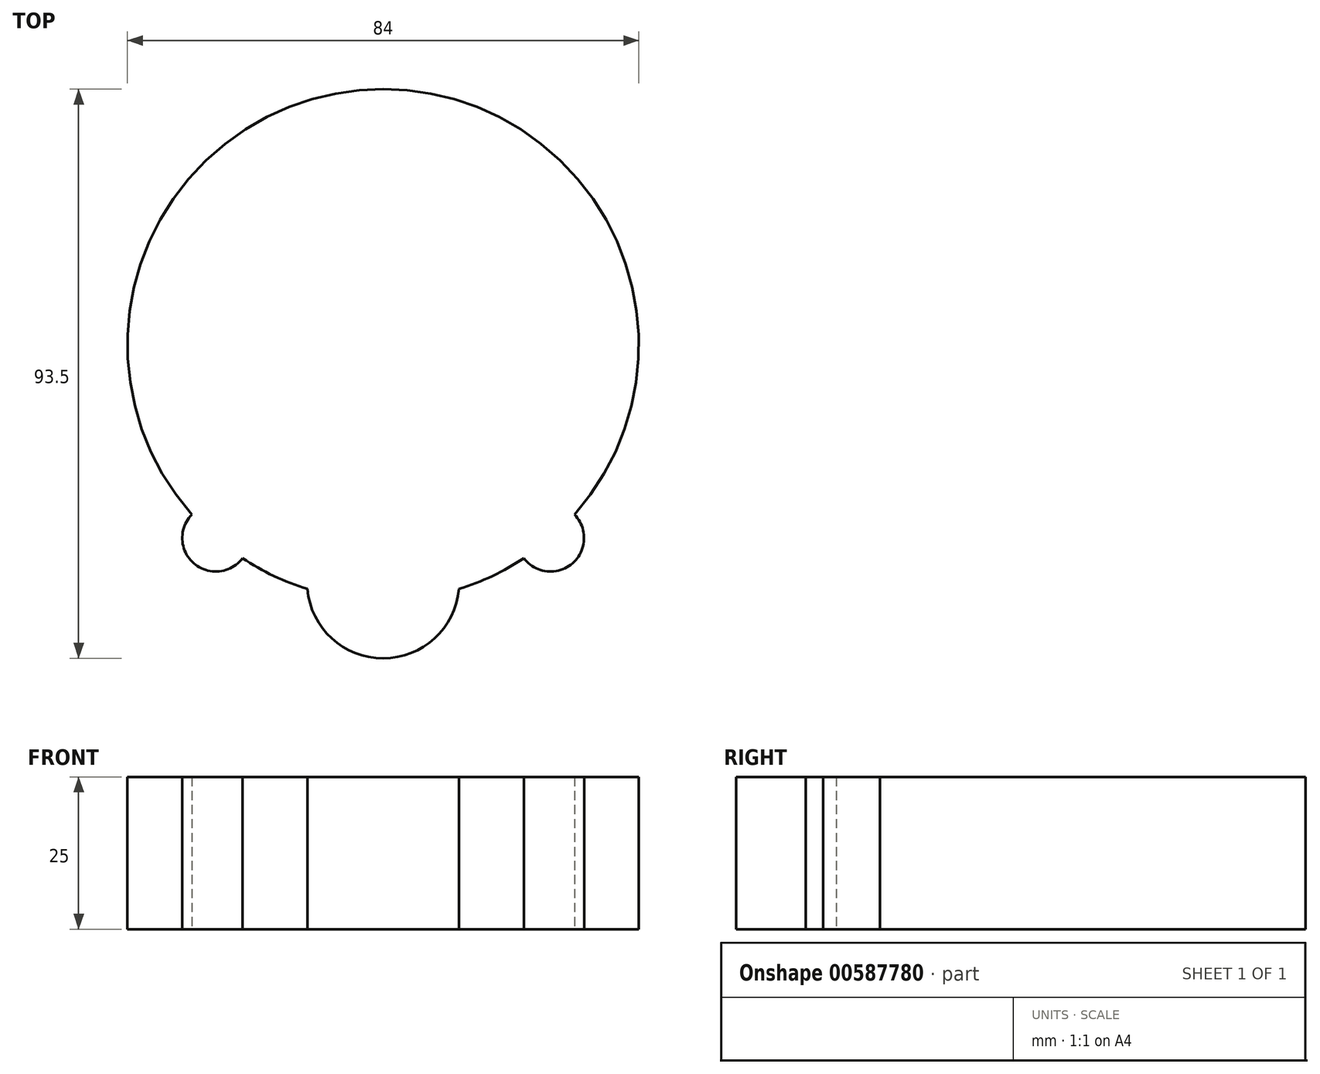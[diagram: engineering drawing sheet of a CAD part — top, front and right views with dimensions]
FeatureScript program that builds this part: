
annotation { "Feature Type Name" : "Feature", "Feature Type Description" : "" }
export const myFeature = defineFeature(function(context is Context, id is Id, definition is map)
    precondition{}
    {
        {
            var Q0;
            Q0=qCreatedBy(makeId("Top.planeOp"),FACE);
            var sketch = newSketch(context, id + "F0", { "sketchPlane" : qUnion([Q0])});
            skCircle(sketch, "E0", {"center": v(0, 0) * mm, "radius": 42 * mm});
            skCircle(sketch, "E1", {"center": v(27.5, -31.75) * mm, "radius": 5.5 * mm});
            skCircle(sketch, "E2", {"center": v(-27.5, -31.75) * mm, "radius": 5.5 * mm});
            skCircle(sketch, "E3", {"center": v(0, -39) * mm, "radius": 12.5 * mm});
            skSolve(sketch);
        }
        {
            var Q0;
            Q0 = qSketchRegion(id + "F0", true);
            extrude(context, id + "F1", {"entities" : qUnion([Q0]), "depth" : 25 * mm, "offsetDistance" : 25 * mm});
        }
    });
